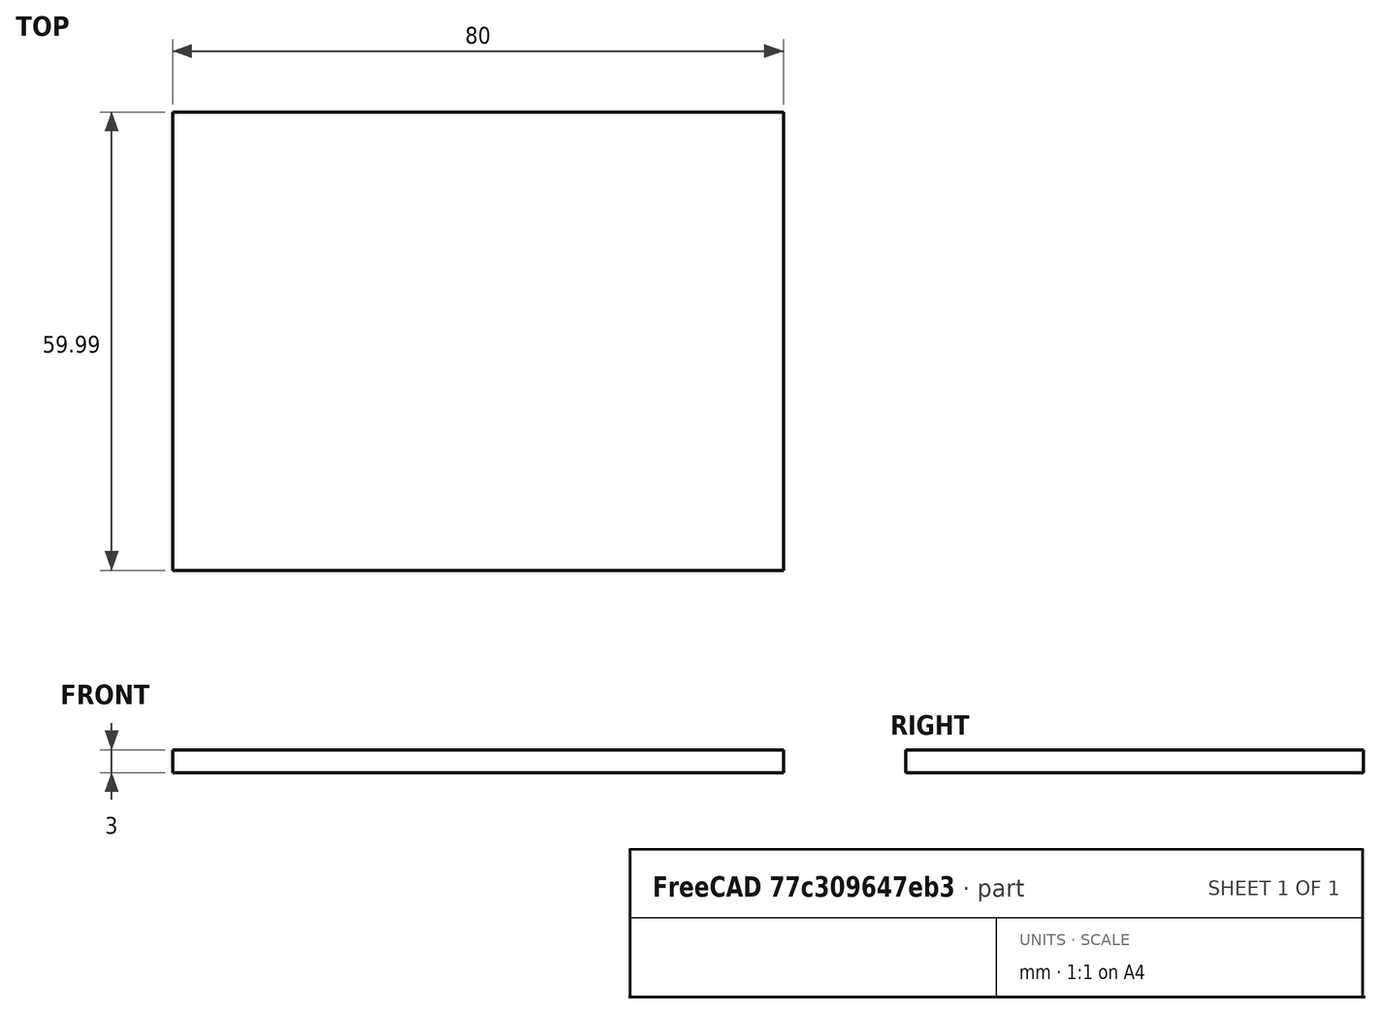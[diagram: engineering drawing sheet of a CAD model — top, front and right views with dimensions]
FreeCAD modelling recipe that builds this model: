
FCSTD DOCUMENT  (FreeCAD 0.19R24291 (Git))
Label: protoboard
License: All rights reserved
LicenseURL: http://en.wikipedia.org/wiki/All_rights_reserved
objects: TechDraw::DrawProjGroupItem×3, TechDraw::DrawViewDimension×3, Sketcher::SketchObject×1, PartDesign::Pad×1, PartDesign::Body×1, TechDraw::DrawSVGTemplate×1, TechDraw::DrawProjGroup×1, TechDraw::DrawPage×1
note: 4 computed .brp shape members not serialized (recipe doc carries the construction recipe); baked Part::Feature solids carry a one-line shape summary decoded from their .brp

FEATURE [Sketcher::SketchObject] Sketch
  FullyConstrained = false
  MapMode = 5
  Support = -> [XY_Plane]
  sketch-geometry (4):
    g0: LineSegment StartX=-46.7569 StartY=40.5161 StartZ=0 EndX=33.2431 EndY=40.5161 EndZ=0
    g1: LineSegment StartX=33.2431 StartY=40.5161 StartZ=0 EndX=33.2431 EndY=-19.4739 EndZ=0
    g2: LineSegment StartX=33.2431 StartY=-19.4739 StartZ=0 EndX=-46.7569 EndY=-19.4739 EndZ=0
    g3: LineSegment StartX=-46.7569 StartY=-19.4739 StartZ=0 EndX=-46.7569 EndY=40.5161 EndZ=0
  constraints (10):
    c: Coincident(g0,g1)
    c: Coincident(g1,g2)
    c: Coincident(g2,g3)
    c: Coincident(g3,g0)
    c: Horizontal(g0)
    c: Horizontal(g2)
    c: Vertical(g1)
    c: Vertical(g3)
    c: DistanceX(g0,g0) = 80
    c: DistanceY(g1,g1) = 59.99
FEATURE [PartDesign::Pad] Pad
  Direction = (1,1,1)
  Length = 3
  Length2 = 100
  Profile = -> Sketch
  Type = 0
FEATURE [PartDesign::Body] Body
  Group = -> [Sketch,Pad]
  Origin = -> Origin
  Tip = -> Pad
FEATURE [TechDraw::DrawSVGTemplate] Template
  EditableTexts = Designed_by_Name=Designed by Name; Drawing_number=Drawing number; FC-Date=Date; FC-SC=Scale; FC-SH=Sheet; FC-Title=Title; Subtitle=Subtitle; Weight=Weight
  Height = 210
  Orientation = 1
  Width = 297
FEATURE [TechDraw::DrawProjGroupItem] ProjItem  label="Front"
  CoarseView = false
  Direction = (0,0,1)
  Focus = 100
  HardHidden = false
  IsoCount = 0
  IsoHidden = false
  IsoVisible = false
  LockPosition = true
  Perspective = false
  Rotation = 0
  RotationVector = (1,0,0)
  ScaleType = 2
  SeamHidden = false
  SeamVisible = true
  SmoothHidden = false
  SmoothVisible = true
  Source = -> [Body]
  Type = 0
  X = 0
  XDirection = (1,0,0)
  Y = 0
FEATURE [TechDraw::DrawProjGroupItem] ProjItem001  label="Left"
  CoarseView = false
  Direction = (-1,0,1e-16)
  Focus = 100
  HardHidden = false
  IsoCount = 0
  IsoHidden = false
  IsoVisible = false
  LockPosition = false
  Perspective = false
  Rotation = 0
  RotationVector = (1,0,0)
  ScaleType = 2
  SeamHidden = false
  SeamVisible = true
  SmoothHidden = false
  SmoothVisible = true
  Source = -> [Body]
  Type = 1
  X = 56.7161
  XDirection = (1e-16,0,1)
  Y = 0
FEATURE [TechDraw::DrawProjGroupItem] ProjItem002  label="Top"
  CoarseView = false
  Direction = (0,1,0)
  Focus = 100
  HardHidden = false
  IsoCount = 0
  IsoHidden = false
  IsoVisible = false
  LockPosition = false
  Perspective = false
  Rotation = 0
  RotationVector = (1,0,0)
  ScaleType = 2
  SeamHidden = false
  SeamVisible = true
  SmoothHidden = false
  SmoothVisible = true
  Source = -> [Body]
  Type = 4
  X = 0
  XDirection = (1,0,0)
  Y = -103.485
FEATURE [TechDraw::DrawProjGroup] ProjGroup
  Anchor = -> ProjItem
  AutoDistribute = true
  LockPosition = false
  ProjectionType = 0
  Rotation = 0
  ScaleType = 0
  Source = -> [Body]
  Views = -> [ProjItem,ProjItem001,ProjItem002]
  X = 88.7104
  Y = 147.412
  spacingX = 15
  spacingY = 15
FEATURE [TechDraw::DrawViewDimension] Dimension
  Arbitrary = false
  ArbitraryTolerances = false
  EqualTolerance = true
  FormatSpec = %.2f
  FormatSpecOverTolerance = %+.2f
  FormatSpecUnderTolerance = %+.2f
  Inverted = false
  LockPosition = false
  MeasureType = 1
  OverTolerance = 0
  References2D = -> [ProjItem]
  Rotation = 0
  ScaleType = 0
  TheoreticalExact = false
  Type = 1
  UnderTolerance = 0
  X = -1.47265
  Y = -41.7762
FEATURE [TechDraw::DrawViewDimension] Dimension001
  Arbitrary = false
  ArbitraryTolerances = false
  EqualTolerance = true
  FormatSpec = %.2f
  FormatSpecOverTolerance = %+.2f
  FormatSpecUnderTolerance = %+.2f
  Inverted = false
  LockPosition = false
  MeasureType = 1
  OverTolerance = 0
  References2D = -> [ProjItem]
  Rotation = 0
  ScaleType = 0
  TheoreticalExact = false
  Type = 2
  UnderTolerance = 0
  X = -52.3703
  Y = 1.76718
FEATURE [TechDraw::DrawViewDimension] Dimension002
  Arbitrary = false
  ArbitraryTolerances = false
  EqualTolerance = true
  FormatSpec = %.2f
  FormatSpecOverTolerance = %+.2f
  FormatSpecUnderTolerance = %+.2f
  Inverted = false
  LockPosition = false
  MeasureType = 1
  OverTolerance = 0
  References2D = -> [ProjItem001]
  Rotation = 0
  ScaleType = 0
  TheoreticalExact = false
  Type = 1
  UnderTolerance = 0
  X = -0.432208
  Y = -40.2599
FEATURE [TechDraw::DrawPage] Page
  KeepUpdated = true
  NextBalloonIndex = 1
  ProjectionType = 0
  Template = -> Template
  Views = -> [ProjGroup,Dimension,Dimension001,Dimension002]
